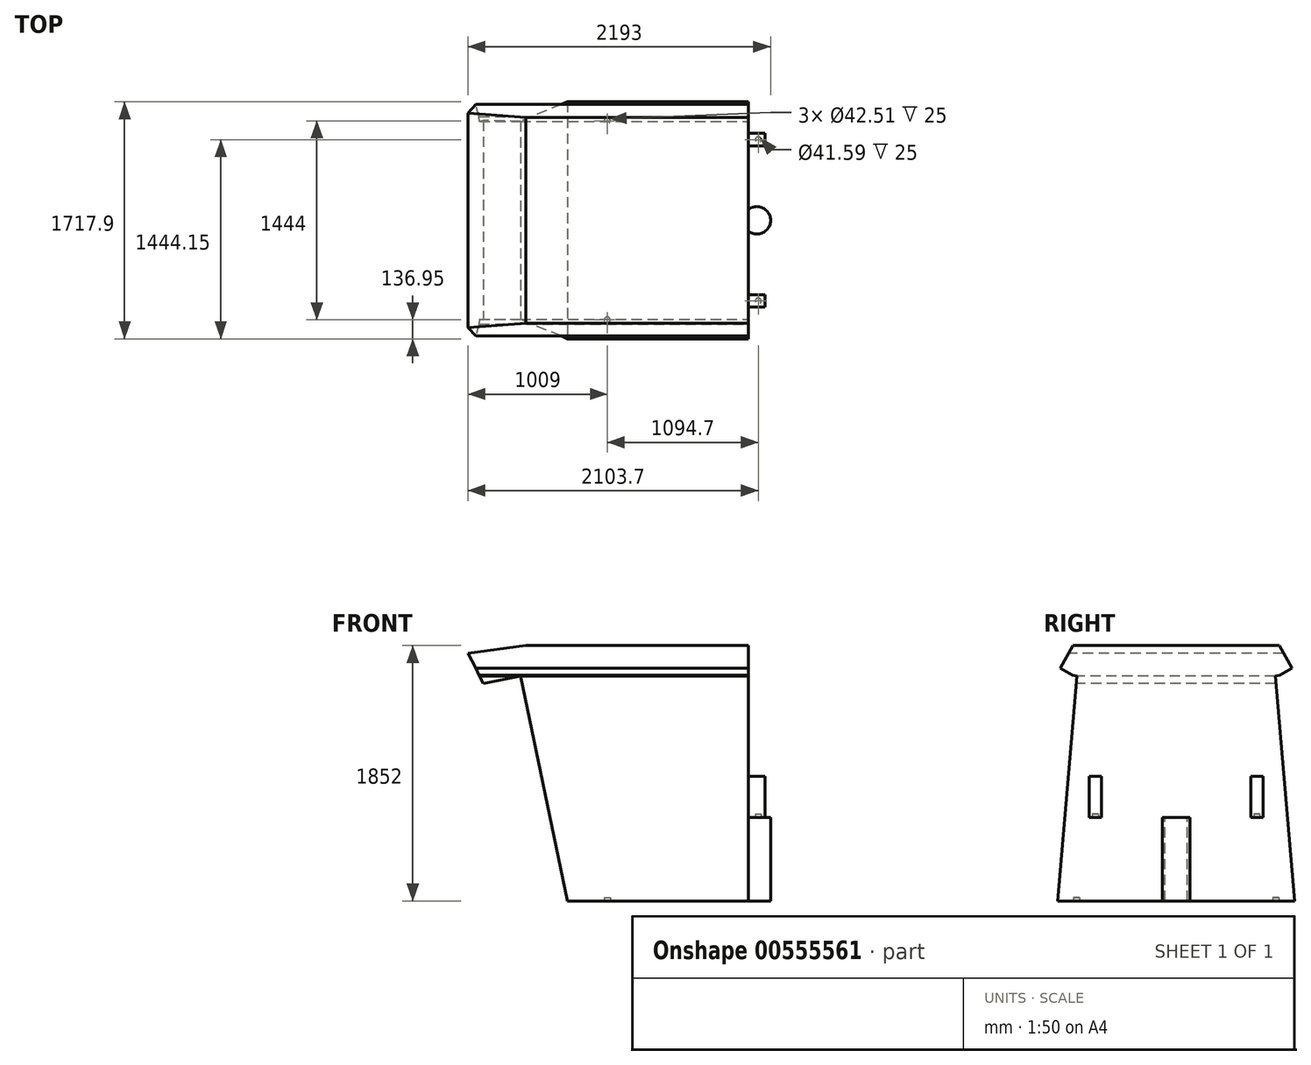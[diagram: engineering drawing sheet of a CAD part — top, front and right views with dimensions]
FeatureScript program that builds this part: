
annotation { "Feature Type Name" : "Feature", "Feature Type Description" : "" }
export const myFeature = defineFeature(function(context is Context, id is Id, definition is map)
    precondition{}
    {
        {
            var Q0;
            Q0=qCreatedBy(makeId("Top.planeOp"),FACE);
            var sketch = newSketch(context, id + "F0", { "sketchPlane" : qUnion([Q0])});
            skLineSegment(sketch, "E0.bottom", {"start": v(-1016.5, 858.95) * mm, "end": v(1016.5, 858.95) * mm});
            skLineSegment(sketch, "E0.top", {"start": v(-1016.5, -858.95) * mm, "end": v(1016.5, -858.95) * mm});
            skLineSegment(sketch, "E0.left", {"start": v(-1016.5, 858.95) * mm, "end": v(-1016.5, -858.95) * mm});
            skLineSegment(sketch, "E0.right", {"start": v(1016.5, 858.95) * mm, "end": v(1016.5, -858.95) * mm});
            skSolve(sketch);
        }
        {
            var Q0;
            Q0 = qSketchRegion(id + "F0", true);
            extrude(context, id + "F1", {"entities" : qUnion([Q0]), "depth" : 1852 * mm, "offsetDistance" : 25 * mm});
        }
        {
            var Q0;
            Q0=makeQuery(id+"F1.opExtrude","SWEPT_FACE",FACE,{"disambiguationData":[OSD([sQuery(id+"F0.wireOp",EDGE,"E0.top")])]});
            var sketch = newSketch(context, id + "F2", { "sketchPlane" : qUnion([Q0])});
            skLineSegment(sketch, "E1", {"start": v(-294.5, 0) * mm, "end": v(-636.5, 1632) * mm});
            skLineSegment(sketch, "E2", {"start": v(-636.5, 1632) * mm, "end": v(-904.44, 1575.85) * mm});
            skLineSegment(sketch, "E3", {"start": v(-904.44, 1575.85) * mm, "end": v(-1016.5, 1796.96) * mm});
            skLineSegment(sketch, "E4", {"start": v(-1016.5, 1796.96) * mm, "end": v(-598.8, 1852) * mm});
            skLineSegment(sketch, "E5", {"start": v(-598.8, 1852) * mm, "end": v(-1016.5, 1852) * mm});
            skLineSegment(sketch, "E6", {"start": v(-1016.5, 1852) * mm, "end": v(-1016.5, 0) * mm});
            skLineSegment(sketch, "E7", {"start": v(-1016.5, 0) * mm, "end": v(-294.5, 0) * mm});
            skSolve(sketch);
        }
        {
            var Q0;
            Q0 = qSketchRegion(id + "F2", true);
            extrude(context, id + "F3", {"entities" : qUnion([Q0]), "operationType" : NewBodyOperationType.REMOVE, "endBound" : BoundingType.THROUGH_ALL, "oppositeDirection" : true, "depth" : 25 * mm, "offsetDistance" : 25 * mm});
        }
        {
            var Q0;
            Q0=makeQuery(id+"F1.opExtrude","SWEPT_FACE",FACE,{"disambiguationData":[OSD([sQuery(id+"F0.wireOp",EDGE,"E0.right")])]});
            var sketch = newSketch(context, id + "F4", { "sketchPlane" : qUnion([Q0])});
            skLineSegment(sketch, "E8", {"start": v(-858.95, 0) * mm, "end": v(-718.08, 1632) * mm});
            skLineSegment(sketch, "E9", {"start": v(-718.08, 1632) * mm, "end": v(-751.5, 1637.4) * mm});
            skLineSegment(sketch, "E10", {"start": v(-751.5, 1637.4) * mm, "end": v(-839.76, 1686.55) * mm});
            skLineSegment(sketch, "E11", {"start": v(-839.76, 1686.55) * mm, "end": v(-747.6, 1852) * mm});
            skLineSegment(sketch, "E12", {"start": v(-747.6, 1852) * mm, "end": v(-858.95, 1852) * mm});
            skLineSegment(sketch, "E13", {"start": v(-858.95, 1852) * mm, "end": v(-858.95, 0) * mm});
            skLineSegment(sketch, "E14", {"start": v(858.95, 0) * mm, "end": v(718.08, 1632) * mm});
            skLineSegment(sketch, "E15", {"start": v(718.08, 1632) * mm, "end": v(751.5, 1637.4) * mm});
            skLineSegment(sketch, "E16", {"start": v(751.5, 1637.4) * mm, "end": v(839.76, 1686.55) * mm});
            skLineSegment(sketch, "E17", {"start": v(839.76, 1686.55) * mm, "end": v(747.6, 1852) * mm});
            skLineSegment(sketch, "E18", {"start": v(747.6, 1852) * mm, "end": v(858.95, 1852) * mm});
            skLineSegment(sketch, "E19", {"start": v(858.95, 1852) * mm, "end": v(858.95, 0) * mm});
            skSolve(sketch);
        }
        {
            var Q0;
            Q0 = qSketchRegion(id + "F4", true);
            extrude(context, id + "F5", {"entities" : qUnion([Q0]), "operationType" : NewBodyOperationType.REMOVE, "endBound" : BoundingType.THROUGH_ALL, "oppositeDirection" : true, "depth" : 25 * mm, "offsetDistance" : 25 * mm});
        }
        {
            var Q0;
            Q0=makeQuery(id+"F1.opExtrude","SWEPT_FACE",FACE,{"disambiguationData":[OSD([sQuery(id+"F0.wireOp",EDGE,"E0.right")])]});
            var sketch = newSketch(context, id + "F6", { "sketchPlane" : qUnion([Q0])});
            skLineSegment(sketch, "E20.bottom", {"start": v(-630.2, 905) * mm, "end": v(-540.2, 905) * mm});
            skLineSegment(sketch, "E20.top", {"start": v(-630.2, 605) * mm, "end": v(-540.2, 605) * mm});
            skLineSegment(sketch, "E20.left", {"start": v(-540.2, 905) * mm, "end": v(-540.2, 605) * mm});
            skLineSegment(sketch, "E20.right", {"start": v(-630.2, 905) * mm, "end": v(-630.2, 605) * mm});
            skLineSegment(sketch, "E21.bottom", {"start": v(540.2, 905) * mm, "end": v(630.2, 905) * mm});
            skLineSegment(sketch, "E21.top", {"start": v(540.2, 605) * mm, "end": v(630.2, 605) * mm});
            skLineSegment(sketch, "E21.left", {"start": v(630.2, 905) * mm, "end": v(630.2, 605) * mm});
            skLineSegment(sketch, "E21.right", {"start": v(540.2, 905) * mm, "end": v(540.2, 605) * mm});
            skLineSegment(sketch, "E22", {"start": v(585.2, 605) * mm, "end": v(585.2, 905) * mm, "construction": true});
            skLineSegment(sketch, "E23", {"start": v(-585.2, 605) * mm, "end": v(-585.2, 905) * mm, "construction": true});
            skSolve(sketch);
        }
        {
            var Q0;
            Q0 = qSketchRegion(id + "F6", true);
            extrude(context, id + "F7", {"entities" : qUnion([Q0]), "operationType" : NewBodyOperationType.ADD, "depth" : 120 * mm, "offsetDistance" : 25 * mm});
        }
        {
            var Q0;
            Q0=makeQuery(id+"F7.opExtrude","SWEPT_FACE",FACE,{"disambiguationData":[OSD([sQuery(id+"F6.wireOp",EDGE,"E21.top")])]});
            var sketch = newSketch(context, id + "F8", { "sketchPlane" : qUnion([Q0])});
            skCircle(sketch, "E24", {"center": v(1087.2, -585.2) * mm, "radius": 20.8 * mm});
            skCircle(sketch, "E25", {"center": v(1087.2, 585.2) * mm, "radius": 21.26 * mm});
            skSolve(sketch);
        }
        {
            var Q0;
            Q0 = qSketchRegion(id + "F8", true);
            extrude(context, id + "F9", {"entities" : qUnion([Q0]), "operationType" : NewBodyOperationType.REMOVE, "oppositeDirection" : true, "depth" : 25 * mm, "offsetDistance" : 25 * mm});
        }
        {
            var Q0;
            Q0=makeQuery(id+"F1.opExtrude","CAP_FACE",FACE,{"disambiguationData":[OSD([sQuery(id+"F0.wireOp",EDGE,"E0.bottom"),sQuery(id+"F0.wireOp",EDGE,"E0.top"),sQuery(id+"F0.wireOp",EDGE,"E0.left"),sQuery(id+"F0.wireOp",EDGE,"E0.right")])],"isStart":true});
            var sketch = newSketch(context, id + "F10", { "sketchPlane" : qUnion([Q0])});
            skCircle(sketch, "E26", {"center": v(-7.5, 722) * mm, "radius": 21.26 * mm});
            skCircle(sketch, "E27", {"center": v(-7.5, -722) * mm, "radius": 21.26 * mm});
            skCircle(sketch, "E28", {"center": v(1087.2, 585.2) * mm, "radius": 8.88 * mm, "construction": true});
            skSolve(sketch);
        }
        {
            var Q0;
            Q0 = qSketchRegion(id + "F10", true);
            extrude(context, id + "F11", {"entities" : qUnion([Q0]), "operationType" : NewBodyOperationType.REMOVE, "oppositeDirection" : true, "depth" : 25 * mm, "offsetDistance" : 25 * mm});
        }
        {
            var Q0;
            Q0=makeQuery(id+"F7.opExtrude","SWEPT_FACE",FACE,{"disambiguationData":[OSD([sQuery(id+"F6.wireOp",EDGE,"E21.top")])]});
            var sketch = newSketch(context, id + "F12", { "sketchPlane" : qUnion([Q0])});
            skCircle(sketch, "E29", {"center": v(1076.5, 0) * mm, "radius": 100 * mm});
            skSolve(sketch);
        }
        {
            var Q0;
            Q0 = qSketchRegion(id + "F12", true);
            var Q1;
            Q1=makeQuery(id+"F1.opExtrude","CAP_FACE",FACE,{"disambiguationData":[OSD([sQuery(id+"F0.wireOp",EDGE,"E0.bottom"),sQuery(id+"F0.wireOp",EDGE,"E0.top"),sQuery(id+"F0.wireOp",EDGE,"E0.left"),sQuery(id+"F0.wireOp",EDGE,"E0.right")])],"isStart":true});
            extrude(context, id + "F13", {"entities" : qUnion([Q0]), "operationType" : NewBodyOperationType.ADD, "endBound" : BoundingType.UP_TO_SURFACE, "depth" : 25 * mm, "endBoundEntityFace" : qUnion([Q1]), "offsetDistance" : 25 * mm});
        }
    });
